# Revit family: TCN-D
name_source: partatom
category: Mechanical Equipment
units: mm (PartAtom-declared; Revit-internal decimal feet)

## family parameters
Always vertical = Yes
Cut with Voids When Loaded = No
Part Type = Normal
Room Calculation Point = No
Round Connector Dimension = Use Radius
Shared = No
Work Plane-Based = No

## types (8) — shared parameters
0 = 0' - 0"
1" = 0' - 1"
1.5 = 0' - 1 1/2"
1/4 = 0' - 0 1/4"
135 = 135.00°
2" = 0' - 2"
2' = 2' - 0"
4" = 0' - 4"
45 = 45.00°
Manufacturer = Loren Cook Company
Model = TCN-D
ONE EIGTH = 0' - 0 1/8"
Type Comments = Tubular Centrifugal Inline Direct Drive Arr. 4
URL = www.lorencook.com

## per-type parameters (varying)
- 60-TCN-D: (A/4)+(A/12)=0' - 6 11/32"; (D+3)/2=0' - 10 3/4"; (D-3)/2=0' - 7 3/4"; (E+3)/2=0' - 8 27/32"; (E-3)/2=0' - 5 27/32"; (J+2")/2=0' - 11 15/32"; -(A/2)=-0' - 9 1/2"; -(C/2)=-0' - 11"; -C+1.5=-1' - 8 1/2"; A=1' - 7"; A/12=0' - 1 19/32"; A/2=0' - 9 1/2"; A/4=0' - 4 3/4"; B=1' - 4"; B-C=-0' - 6"; B/2=0' - 8"; B/3=0' - 5 11/32"; C=1' - 10"; C/2=0' - 11"; C/3*2=-0' - 7 11/32"; D=1' - 6 1/2"; D+3=1' - 9 1/2"; D-3=1' - 3 1/2"; D/2=0' - 9 1/4"; E=1' - 2 11/16"; E+3=1' - 5 11/16"; E-3=0' - 11 11/16"; E/2=0' - 7 11/32"; F=1' - 5 11/16"; G=0' - 10 1/8"; G+SQ=1' - 5 17/32"; G-SQ=0' - 2 23/32"; H=2' - 6 5/8"; H/2=1' - 3 5/16"; J=1' - 8 15/16"; J/2=0' - 10 15/32"; LONG=0' - 10 7/8"; SHORT=0' - 7 1/2"; SQRT((J^2)/2)=0' - 7 13/32"
- 70-TCN-D: (A/4)+(A/12)=0' - 6 11/32"; (D+3)/2=0' - 10 3/4"; (D-3)/2=0' - 7 3/4"; (E+3)/2=0' - 8 27/32"; (E-3)/2=0' - 5 27/32"; (J+2")/2=0' - 11 15/32"; -(A/2)=-0' - 9 1/2"; -(C/2)=-0' - 11"; -C+1.5=-1' - 8 1/2"; A=1' - 7"; A/12=0' - 1 19/32"; A/2=0' - 9 1/2"; A/4=0' - 4 3/4"; B=1' - 4"; B-C=-0' - 6"; B/2=0' - 8"; B/3=0' - 5 11/32"; C=1' - 10"; C/2=0' - 11"; C/3*2=-0' - 7 11/32"; D=1' - 6 1/2"; D+3=1' - 9 1/2"; D-3=1' - 3 1/2"; D/2=0' - 9 1/4"; E=1' - 2 11/16"; E+3=1' - 5 11/16"; E-3=0' - 11 11/16"; E/2=0' - 7 11/32"; F=1' - 5 11/16"; G=0' - 10 1/8"; G+SQ=1' - 5 17/32"; G-SQ=0' - 2 23/32"; H=2' - 6 5/8"; H/2=1' - 3 5/16"; J=1' - 8 15/16"; J/2=0' - 10 15/32"; LONG=0' - 10 7/8"; SHORT=0' - 7 1/2"; SQRT((J^2)/2)=0' - 7 13/32"
- 80-TCN-D: (A/4)+(A/12)=0' - 6 11/32"; (D+3)/2=0' - 10 3/4"; (D-3)/2=0' - 7 3/4"; (E+3)/2=0' - 8 27/32"; (E-3)/2=0' - 5 27/32"; (J+2")/2=0' - 11 15/32"; -(A/2)=-0' - 9 1/2"; -(C/2)=-0' - 11"; -C+1.5=-1' - 8 1/2"; A=1' - 7"; A/12=0' - 1 19/32"; A/2=0' - 9 1/2"; A/4=0' - 4 3/4"; B=1' - 4"; B-C=-0' - 6"; B/2=0' - 8"; B/3=0' - 5 11/32"; C=1' - 10"; C/2=0' - 11"; C/3*2=-0' - 7 11/32"; D=1' - 6 1/2"; D+3=1' - 9 1/2"; D-3=1' - 3 1/2"; D/2=0' - 9 1/4"; E=1' - 2 11/16"; E+3=1' - 5 11/16"; E-3=0' - 11 11/16"; E/2=0' - 7 11/32"; F=1' - 5 11/16"; G=0' - 10 1/8"; G+SQ=1' - 5 17/32"; G-SQ=0' - 2 23/32"; H=2' - 6 5/8"; H/2=1' - 3 5/16"; J=1' - 8 15/16"; J/2=0' - 10 15/32"; LONG=0' - 10 7/8"; SHORT=0' - 7 1/2"; SQRT((J^2)/2)=0' - 7 13/32"
- 100-TCN-D: (A/4)+(A/12)=0' - 6 11/32"; (D+3)/2=0' - 10 3/4"; (D-3)/2=0' - 7 3/4"; (E+3)/2=0' - 8 27/32"; (E-3)/2=0' - 5 27/32"; (J+2")/2=0' - 11 15/32"; -(A/2)=-0' - 9 1/2"; -(C/2)=-0' - 11"; -C+1.5=-1' - 8 1/2"; A=1' - 7"; A/12=0' - 1 19/32"; A/2=0' - 9 1/2"; A/4=0' - 4 3/4"; B=1' - 4"; B-C=-0' - 6"; B/2=0' - 8"; B/3=0' - 5 11/32"; C=1' - 10"; C/2=0' - 11"; C/3*2=-0' - 7 11/32"; D=1' - 6 1/2"; D+3=1' - 9 1/2"; D-3=1' - 3 1/2"; D/2=0' - 9 1/4"; E=1' - 2 11/16"; E+3=1' - 5 11/16"; E-3=0' - 11 11/16"; E/2=0' - 7 11/32"; F=1' - 5 11/16"; G=0' - 10 1/8"; G+SQ=1' - 5 17/32"; G-SQ=0' - 2 23/32"; H=2' - 6 5/8"; H/2=1' - 3 5/16"; J=1' - 8 15/16"; J/2=0' - 10 15/32"; LONG=0' - 10 7/8"; SHORT=0' - 7 1/2"; SQRT((J^2)/2)=0' - 7 13/32"
- 120-TCN-D: (A/4)+(A/12)=0' - 7"; (D+3)/2=0' - 11 1/4"; (D-3)/2=0' - 8 1/4"; (E+3)/2=0' - 9 9/16"; (E-3)/2=0' - 6 9/16"; (J+2")/2=1' - 0 15/32"; -(A/2)=-0' - 10 1/2"; -(C/2)=-0' - 11 1/2"; -C+1.5=-1' - 9 1/2"; A=1' - 9"; A/12=0' - 1 3/4"; A/2=0' - 10 1/2"; A/4=0' - 5 1/4"; B=1' - 6"; B-C=-0' - 5"; B/2=0' - 9"; B/3=0' - 6"; C=1' - 11"; C/2=0' - 11 1/2"; C/3*2=-0' - 7 21/32"; D=1' - 7 1/2"; D+3=1' - 10 1/2"; D-3=1' - 4 1/2"; D/2=0' - 9 3/4"; E=1' - 4 1/8"; E+3=1' - 7 1/8"; E-3=1' - 1 1/8"; E/2=0' - 8 1/16"; F=1' - 7 1/8"; G=0' - 10 7/8"; G+SQ=1' - 7"; G-SQ=0' - 2 3/4"; H=2' - 8 3/16"; H/2=1' - 4 3/32"; J=1' - 10 15/16"; J/2=0' - 11 15/32"; LONG=0' - 11 3/8"; SHORT=0' - 8"; SQRT((J^2)/2)=0' - 8 1/8"
- 135-TCN-D: (A/4)+(A/12)=0' - 8"; (D+3)/2=0' - 11 1/2"; (D-3)/2=0' - 8 1/2"; (E+3)/2=0' - 10 5/8"; (E-3)/2=0' - 7 5/8"; (J+2")/2=1' - 2"; -(A/2)=-1' - 0"; -(C/2)=-1' - 0 1/4"; -C+1.5=-1' - 11"; A=2' - 0"; A/12=0' - 2"; A/2=1' - 0"; A/4=0' - 6"; B=1' - 9"; B-C=-0' - 3 1/2"; B/2=0' - 10 1/2"; B/3=0' - 7"; C=2' - 0 1/2"; C/2=1' - 0 1/4"; C/3*2=-0' - 8 5/32"; D=1' - 8"; D+3=1' - 11"; D-3=1' - 5"; D/2=0' - 10"; E=1' - 6 1/4"; E+3=1' - 9 1/4"; E-3=1' - 3 1/4"; E/2=0' - 9 1/8"; F=1' - 9 1/4"; G=1' - 1 3/8"; G+SQ=1' - 10 9/16"; G-SQ=0' - 4 3/16"; H=3' - 0 3/4"; H/2=1' - 6 3/8"; J=2' - 2"; J/2=1' - 1"; LONG=1' - 0 1/8"; SHORT=0' - 7 3/4"; SQRT((J^2)/2)=0' - 9 3/16"
- 150-TCN-D: (A/4)+(A/12)=0' - 9"; (D+3)/2=1' - 0 3/4"; (D-3)/2=0' - 9 3/4"; (E+3)/2=0' - 11 11/16"; (E-3)/2=0' - 8 11/16"; (J+2")/2=1' - 3 1/2"; -(A/2)=-1' - 1 1/2"; -(C/2)=-1' - 1 5/8"; -C+1.5=-2' - 1 3/4"; A=2' - 3"; A/12=0' - 2 1/4"; A/2=1' - 1 1/2"; A/4=0' - 6 3/4"; B=2' - 0"; B-C=-0' - 3 1/4"; B/2=1' - 0"; B/3=0' - 8"; C=2' - 3 1/4"; C/2=1' - 1 5/8"; C/3*2=-0' - 9 3/32"; D=1' - 10 1/2"; D+3=2' - 1 1/2"; D-3=1' - 7 1/2"; D/2=0' - 11 1/4"; E=1' - 8 3/8"; E+3=1' - 11 3/8"; E-3=1' - 5 3/8"; E/2=0' - 10 3/16"; F=1' - 11 3/8"; G=1' - 2 1/2"; G+SQ=2' - 0 3/4"; G-SQ=0' - 4 1/4"; H=3' - 7 1/4"; H/2=1' - 9 5/8"; J=2' - 5"; J/2=1' - 2 1/2"; LONG=1' - 1 1/2"; SHORT=0' - 8 7/8"; SQRT((J^2)/2)=0' - 10 1/4"
- 165-TCN-D: (A/4)+(A/12)=0' - 9 21/32"; (D+3)/2=1' - 1"; (D-3)/2=0' - 10"; (E+3)/2=1' - 0 7/8"; (E-3)/2=0' - 9 7/8"; (J+2")/2=1' - 5 3/16"; -(A/2)=-1' - 2 1/2"; -(C/2)=-1' - 2 3/8"; -C+1.5=-2' - 3 1/4"; A=2' - 5"; A/12=0' - 2 13/32"; A/2=1' - 2 1/2"; A/4=0' - 7 1/4"; B=2' - 2"; B-C=-0' - 2 3/4"; B/2=1' - 1"; B/3=0' - 8 21/32"; C=2' - 4 3/4"; C/2=1' - 2 3/8"; C/3*2=-0' - 9 19/32"; D=1' - 11"; D+3=2' - 2"; D-3=1' - 8"; D/2=0' - 11 1/2"; E=1' - 10 3/4"; E+3=2' - 1 3/4"; E-3=1' - 7 3/4"; E/2=0' - 11 3/8"; F=2' - 2 7/8"; G=1' - 3 3/4"; G+SQ=2' - 3 3/16"; G-SQ=0' - 4 5/16"; H=3' - 9 3/4"; H/2=1' - 10 7/8"; J=2' - 8 3/8"; J/2=1' - 4 3/16"; LONG=1' - 2 1/4"; SHORT=0' - 8 5/8"; SQRT((J^2)/2)=0' - 11 7/16"

## geometry (parser evidence)
native form markers: Sweep x2
no freeform markers — native parametric forms only
